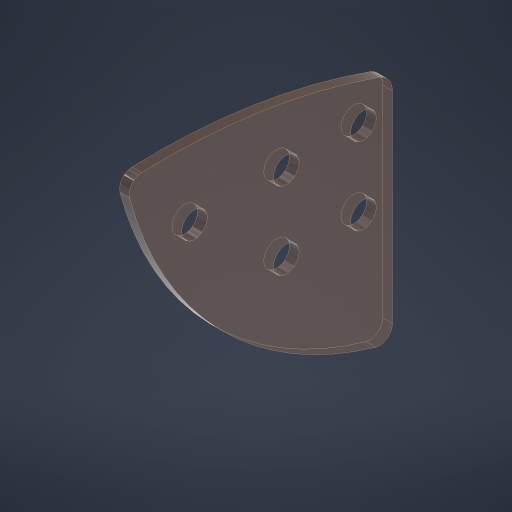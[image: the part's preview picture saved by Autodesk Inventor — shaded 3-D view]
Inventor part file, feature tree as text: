
AUTODESK INVENTOR PART (.ipt)
format: ipt  version: 2024 (Build 280153000, 153)  size: 250,880 bytes
history: native  units: in
note: dims shown in document units (in); Inventor stores cm internally (conversion verified against a paired STEP export)
features: sketch x2, extrude x1, hole x1
ambient origin geometry x8: Origin, YZ Plane, XZ Plane, XY Plane, X Axis, Y Axis, Z Axis, Center Point
bodies: Solid1 (feature_tree)
feature tree (4):
  extrude  "Extrusion1"  Depth=0.0625in TaperAngle=0.0deg
  hole  "Hole1"  [1 undecoded]
  sketch  "Sketch1"  dims[d1=0.875in d7=0.0625in d8=0.0in]
  sketch  "Sketch2"  dims[d13=0.1875in d14=0.5in d15=0.25in d16=0.5in d17=0.167in d18=0.75in d19=0.375in d20=0.25in d21=0.5635in d22=1.0in d23=0.8108in d49=0.188in d50=45.0deg d51=0.403in d52=45.0deg d55=1.5in d57=0.0833in d58=0.125in]
note: 1 required parameter value undecoded (feature->parameter linkage not recoverable at this tier; creation-order binding heuristic only, values carry confidence <= 0.55)
